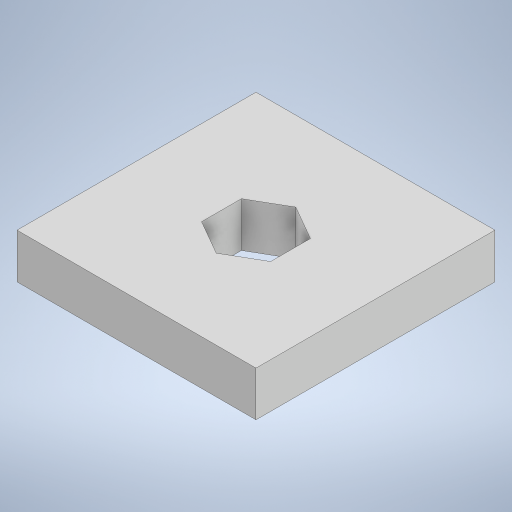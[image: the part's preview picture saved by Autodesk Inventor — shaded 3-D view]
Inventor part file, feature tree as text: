
AUTODESK INVENTOR PART (.ipt)
format: ipt  version: 2023 (Build 270158000, 158)  size: 207,872 bytes
history: native  units: in
note: dims shown in document units (in); Inventor stores cm internally (conversion verified against a paired STEP export)
features: extrude x1, sketch x1
ambient origin geometry x8: Origin, YZ Plane, XZ Plane, XY Plane, X Axis, Y Axis, Z Axis, Center Point
bodies: Solid1 (feature_tree)
feature tree (2):
  extrude  "Extrusion1"  Depth=2.0in
  sketch  "Sketch1"  dims[d0=2.0in d1=2.0in d4=0.5in d5=0.375in d6=0.0in d12=0.5in d13=0.0344in d14=0.5in d15=0.0344in]
